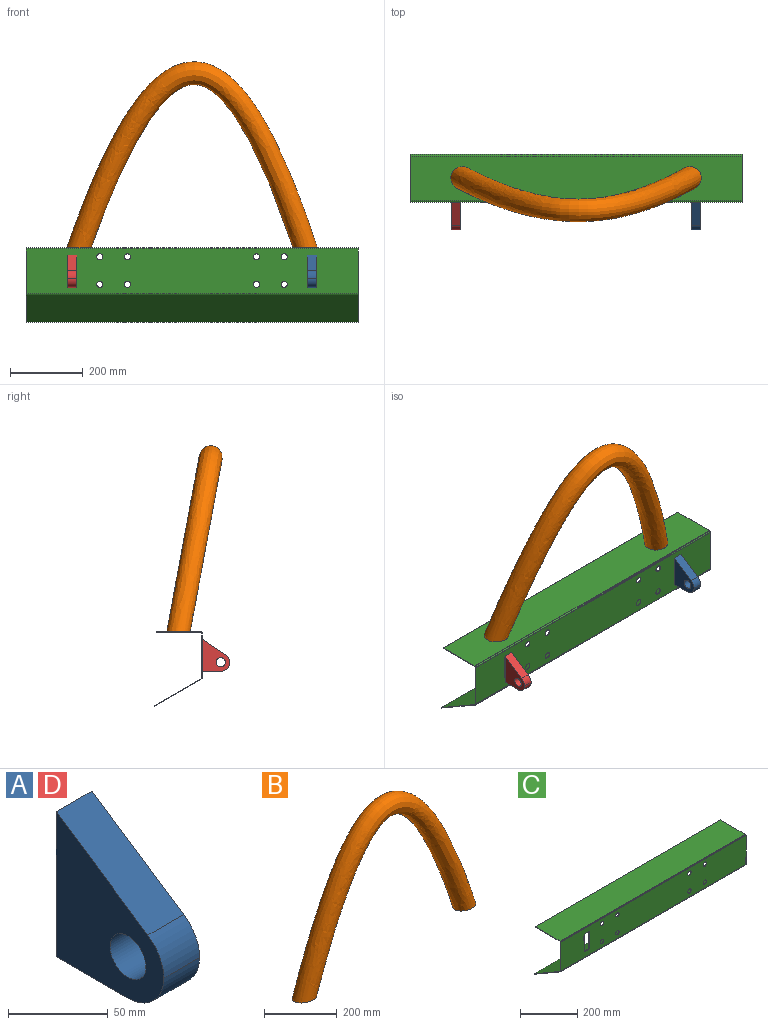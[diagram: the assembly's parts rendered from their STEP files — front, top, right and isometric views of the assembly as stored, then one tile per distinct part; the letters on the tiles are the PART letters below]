
ASSEMBLY  parts=4 mates=3
PART A: 8 faces, bbox 25.4x76.2x88.9 mm
  f0: plane 88.9x76.2mm, normal (-1,0,0), area 4165.3mm2, adj f1,f3,f4,f5,f6,f7
  f1: plane 50.8x25.4mm, normal (0,0,-1), area 1290.3mm2, adj f0,f2,f3,f5
  f2: plane 88.9x76.2mm, normal (1,0,0), area 4165.3mm2, adj f1,f3,f4,f5,f6,f7
  f3: plane 88.9x25.4mm, normal (0,1,0), area 2258.1mm2, adj f0,f1,f2,f4
  f4: plane 64.89x43.26mm, normal (0,-0.55,0.83), area 1980.9mm2, adj f0,f2,f3,f6
  f5: cylinder r=25.4mm len=25.4mm, axis (-1,0,0), area 1002.1mm2, adj f0,f1,f2,f6
  f6: cylinder r=25.4mm len=25.4mm, axis (1,0,0), area 622.7mm2, adj f0,f2,f4,f5
  f7: cylinder r=12.7mm len=25.4mm, axis (-1,0,0), area 2026.8mm2, adj f0,f2
PART B: 3 faces, bbox 695.3x127x549.5 mm
  f0: bspline ~695.33x549.47mm, area 240615mm2, adj f1,f2
  f1: plane 67.27x63.51mm, normal (0,-0.18,-0.98), area 3403.9mm2, adj f0
  f2: plane 66.89x63.51mm, normal (0,-0.18,-0.98), area 3384.9mm2, adj f0
PART C: 34 faces, bbox 914.4x132.8x205.7 mm
  f0: plane 76.2x1.59mm, normal (-1,0,0), area 121mm2, adj f1,f13,f14,f15
  f1: plane 25.4x1.59mm, normal (0,0,-1), area 40.3mm2, adj f0,f2,f14,f15
  f2: plane 76.2x1.59mm, normal (1,0,0), area 121mm2, adj f1,f13,f14,f15
  f3: plane 123.39x1.59mm, normal (1,0,0), area 195.9mm2, adj f14,f15,f22,f30
  f4: plane 123.39x1.59mm, normal (-1,0,0), area 195.9mm2, adj f14,f15,f21,f31
  f5: cylinder r=8.33mm len=16.67mm, axis (0,-1,0), area 83.1mm2, adj f14,f15
  f6: cylinder r=8.33mm len=16.67mm, axis (0,-1,0), area 83.1mm2, adj f14,f15
  f7: cylinder r=8.33mm len=16.67mm, axis (0,-1,0), area 83.1mm2, adj f14,f15
  f8: cylinder r=8.33mm len=16.67mm, axis (0,-1,0), area 83.1mm2, adj f14,f15
  f9: cylinder r=8.33mm len=16.67mm, axis (0,-1,0), area 83.1mm2, adj f14,f15
  f10: cylinder r=8.33mm len=16.67mm, axis (0,-1,0), area 83.1mm2, adj f14,f15
  f11: cylinder r=8.33mm len=16.67mm, axis (0,-1,0), area 83.1mm2, adj f14,f15
  f12: cylinder r=8.33mm len=16.67mm, axis (0,-1,0), area 83.1mm2, adj f14,f15
  f13: plane 25.4x1.59mm, normal (0,0,1), area 40.3mm2, adj f0,f2,f14,f15
  f14: plane 914.4x123.39mm, normal (0,1,0), area 109150.7mm2, adj f0,f1,f2,f3,f4,f5,f6,f7
  f15: plane 914.4x123.39mm, normal (0,-1,0), area 109150.7mm2, adj f0,f1,f2,f3,f4,f5,f6,f7
  f16: plane 914.4x1.59mm, normal (0,1,0), area 1451.6mm2, adj f17,f18,f19,f20
  f17: plane 123.13x1.59mm, normal (1,0,0), area 195.5mm2, adj f16,f19,f20,f22
  f18: plane 123.13x1.59mm, normal (-1,0,0), area 195.5mm2, adj f16,f19,f20,f21
  f19: plane 914.4x123.13mm, normal (0,0,-1), area 112586.9mm2, adj f16,f17,f18,f24
  f20: plane 914.4x123.13mm, normal (0,0,1), area 112586.9mm2, adj f16,f17,f18,f23
  f21: plane 3.87x3.87mm, normal (-1,0,0), area 7.7mm2, adj f4,f18,f23,f24
  f22: plane 3.87x3.87mm, normal (1,0,0), area 7.7mm2, adj f3,f17,f23,f24
  f23: cylinder r=3.87mm len=914.4mm, axis (-1,0,0), area 5563.6mm2, adj f15,f20,f21,f22
  f24: cylinder r=2.29mm len=914.4mm, axis (-1,0,0), area 3283.5mm2, adj f14,f19,f21,f22
  f25: plane 914.4x1.38mm, normal (0,0.87,-0.5), area 1451.6mm2, adj f26,f27,f28,f29
  f26: plane 130.84x76.46mm, normal (-1,0,0), area 238.4mm2, adj f25,f28,f29,f31
  f27: plane 130.84x76.46mm, normal (1,0,0), area 238.4mm2, adj f25,f28,f29,f30
  f28: plane 914.4x130.05mm, normal (0,0.5,0.87), area 137309.6mm2, adj f25,f26,f27,f33
  f29: plane 914.4x130.05mm, normal (0,-0.5,-0.87), area 137309.6mm2, adj f25,f26,f27,f32
  f30: plane 3.35x2.73mm, normal (1,0,0), area 5.1mm2, adj f3,f27,f32,f33
  f31: plane 3.35x2.73mm, normal (-1,0,0), area 5.1mm2, adj f4,f26,f32,f33
  f32: cylinder r=3.87mm len=914.4mm, axis (1,0,0), area 3709.1mm2, adj f15,f29,f30,f31
  f33: cylinder r=2.29mm len=914.4mm, axis (1,0,0), area 2189mm2, adj f14,f28,f30,f31
PART D: same geometry as A
PLACE A t=(537.71,0,-14.8)mm
PLACE B rot(axis=(1,0,0),10.5deg) t=(193.79,2.11,395.75)mm
PLACE C t=(-8.71,6.35,36.41)mm
PLACE D t=(-122.69,0,-14.8)mm
MATE fastened B.f1 <-> C.f20  axis (0,0,-1) through (-139.16,65.44,53.5)mm
MATE fastened D.f3 <-> C.f15  axis (0,1,0) through (-158.21,0,-12.07)mm
MATE fastened A.f3 <-> C.f15  axis (0,1,0) through (502.19,0,-12.07)mm
